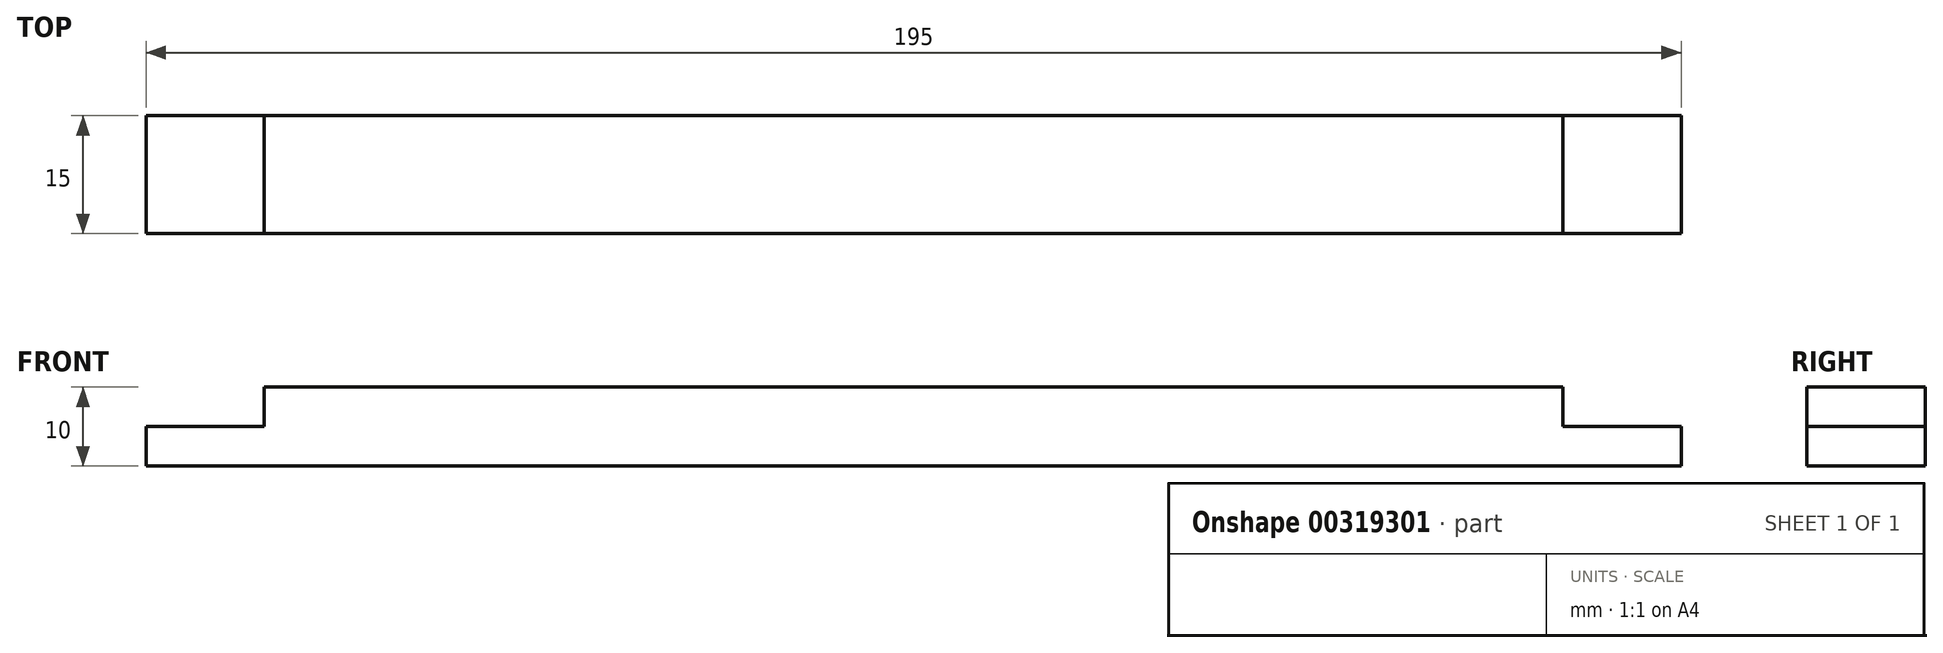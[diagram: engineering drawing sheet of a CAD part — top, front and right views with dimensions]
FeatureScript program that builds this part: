
annotation { "Feature Type Name" : "Feature", "Feature Type Description" : "" }
export const myFeature = defineFeature(function(context is Context, id is Id, definition is map)
    precondition{}
    {
        {
            var Q0;
            Q0=qCreatedBy(makeId("Front.planeOp"),FACE);
            var sketch = newSketch(context, id + "F0", { "sketchPlane" : qUnion([Q0])});
            skLineSegment(sketch, "E0", {"start": v(-100.36, 0) * mm, "end": v(64.64, 0) * mm});
            skLineSegment(sketch, "E1", {"start": v(64.64, 0) * mm, "end": v(64.64, -5) * mm});
            skLineSegment(sketch, "E2", {"start": v(64.64, -5) * mm, "end": v(79.64, -5) * mm});
            skLineSegment(sketch, "E3", {"start": v(79.64, -5) * mm, "end": v(79.64, -10) * mm});
            skLineSegment(sketch, "E4", {"start": v(79.64, -10) * mm, "end": v(-115.36, -10) * mm});
            skLineSegment(sketch, "E5", {"start": v(-115.36, -10) * mm, "end": v(-115.36, -5) * mm});
            skLineSegment(sketch, "E6", {"start": v(-115.36, -5) * mm, "end": v(-100.36, -5) * mm});
            skLineSegment(sketch, "E7", {"start": v(-100.36, -5) * mm, "end": v(-100.36, 0) * mm});
            skSolve(sketch);
        }
        {
            var Q0;
            Q0 = qSketchRegion(id + "F0", true);
            extrude(context, id + "F1", {"entities" : qUnion([Q0]), "depth" : 15 * mm});
        }
    });
